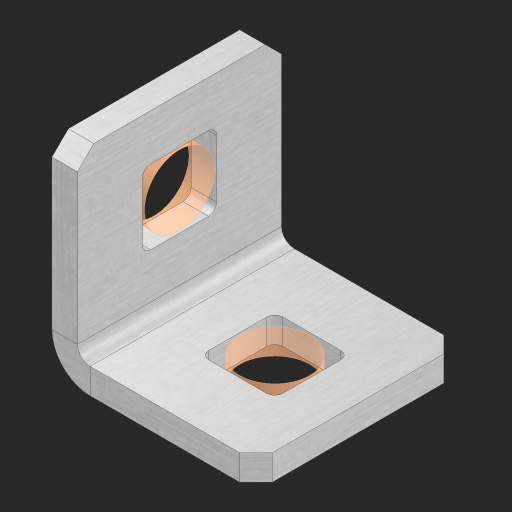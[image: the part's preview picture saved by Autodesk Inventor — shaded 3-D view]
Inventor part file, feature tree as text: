
AUTODESK INVENTOR PART (.ipt)
format: ipt  version: 2023 (Build 270158000, 158)  size: 431,104 bytes
history: native  units: in
note: dims shown in document units (in); Inventor stores cm internally (conversion verified against a paired STEP export)
features: other x76, extrude x71, sheet_metal_op x8, sketch x5, pattern_linear x1, mirror x1, chamfer x1
ambient origin geometry x8: Origin, YZ Plane, XZ Plane, XY Plane, X Axis, Y Axis, Z Axis, Center Point
bodies: Solid1 (feature_tree), Body (feature_tree)
feature tree (163):
  sheet_metal_op  "Flanges"
  sheet_metal_op  "Body Pattern"
  other  "Arc Length"
  pattern_linear  "Notch Pattern"  Spacing1=0.125in  [1 undecoded]
  other  "Diagonal Plane"
  mirror  "Everything Mirrored"
  chamfer  "End Chamfer"
  sketch  "Sketch1"  dims[d0=0.5in]
  other  "Plate1"
  sketch  "Sketch2"  dims[d1=0.5in]
  other  "Plate2"
  sheet_metal_op  "Bend1"
  sheet_metal_op  "Corner1"
  sketch  "Sketch8"  dims[d2=0.0625in]
  sketch  "Sketch9"  dims[d3=0.0625in]
  other  "Srf91"
  sheet_metal_op  "Body Pattern Sketch"
  other  "Srf92"
  sketch  "Sketch13"  dims[d4=0.0312in d5=0.125in d6=0.0625in d7=0.5in d8=90.0deg d9=0.0312in d10=0.25in d11=0.0625in d12=0.0625in d49=0.182in d50=0.02in d52=0.25in d53=0.0625in d54=0.0in d55=0.172in d56=1.0in d57=0.0in d85=0.1473in d86=0.1782in d89=0.0625in d90=0.0in d91=0.04in d92=0.0491in d95=2.5in d96=0.04in d97=0.25in d98=45.0deg d123=0.204in d126=0.0491in d127=0.1473in d128=0.08in d129=0.04in d130=2.5in d131=0.3937in d133=0.5in d134=0.3937in d136=1.0in]
  other  "Srf856"
  other  "Srf857"
  other  "Srf858"
  other  "Srf859"
  other  "Srf860"
  other  "Srf861"
  other  "Srf1275"
  other  "Srf1276"
  other  "Srf1278"
  other  "Srf1279"
  other  "Srf1280"
  other  "Srf1281"
  other  "Srf1282"
  other  "Srf1283"
  other  "Srf1383"
  other  "Srf1384"
  other  "Srf1385"
  other  "Srf1386"
  other  "Srf1387"
  other  "Srf1388"
  other  "Srf1389"
  other  "Srf1390"
  other  "Srf1391"
  other  "Srf1392"
  other  "Srf1393"
  other  "Srf1394"
  other  "Srf1395"
  other  "Srf1396"
  other  "Srf1397"
  other  "Srf1398"
  other  "Srf1399"
  other  "Srf1400"
  other  "Srf1401"
  other  "Srf1402"
  other  "Srf1403"
  other  "Srf1404"
  other  "Srf1405"
  other  "Srf1406"
  other  "Srf1407"
  other  "Srf1408"
  other  "Srf1409"
  other  "Srf1475"
  other  "Srf1476"
  other  "Srf1477"
  other  "Srf1478"
  other  "Srf1479"
  other  "Srf1480"
  other  "Srf1481"
  other  "Srf1482"
  other  "Srf1483"
  other  "Srf1484"
  other  "Srf1485"
  other  "Srf1486"
  other  "Srf1487"
  other  "Srf1488"
  other  "Srf1489"
  other  "Srf1490"
  other  "Srf1491"
  other  "Srf1492"
  other  "Srf1493"
  other  "Srf1494"
  other  "Srf1495"
  other  "Srf1496"
  other  "Srf1497"
  other  "Srf1498"
  other  "Srf1499"
  other  "Srf1500"
  other  "Srf1501"
  other  "Srf1568"
  other  "Srf1569"
  sheet_metal_op  "Body Stamp"
  sheet_metal_op  "Body Circle"
  sheet_metal_op  "Notch"
  extrude  "ExtrusionSrf92"  Depth=0.0625in
  extrude  "ExtrusionSrf856"  Depth=0.5in TaperAngle=90.0deg
  extrude  "ExtrusionSrf857"  Depth=0.25in
  extrude  "ExtrusionSrf858"  Depth=0.0625in
  extrude  "ExtrusionSrf859"  Depth=0.0625in
  extrude  "ExtrusionSrf860"  Depth=0.182in
  extrude  "ExtrusionSrf861"  Depth=0.02in
  extrude  "ExtrusionSrf1275"  Depth=0.25in
  extrude  "ExtrusionSrf1276"  Depth=0.0625in
  extrude  "ExtrusionSrf1277"  TaperAngle=0.0deg  [1 undecoded]
  extrude  "ExtrusionSrf1278"  Depth=0.3937in
  extrude  "ExtrusionSrf1279"  Depth=0.3937in TaperAngle=0.0deg
  extrude  "ExtrusionSrf1280"  Depth=0.3937in
  extrude  "ExtrusionSrf1281"  Depth=0.3937in
  extrude  "ExtrusionSrf1282"  Depth=0.0625in
  extrude  "ExtrusionSrf1383"  Depth=0.3937in TaperAngle=0.0deg
  extrude  "ExtrusionSrf1384"  Depth=0.3937in
  extrude  "ExtrusionSrf1385"  Depth=0.25in TaperAngle=45.0deg
  extrude  "ExtrusionSrf1386"  Depth=0.3937in
  extrude  "ExtrusionSrf1387"  Depth=0.3937in
  extrude  "ExtrusionSrf1388"  Depth=0.3937in
  extrude  "ExtrusionSrf1389"  Depth=0.3937in
  extrude  "ExtrusionSrf1390"  Depth=0.3937in
  extrude  "ExtrusionSrf1391"  Depth=0.3937in
  extrude  "ExtrusionSrf1392"  Depth=0.3937in
  extrude  "ExtrusionSrf1393"  Depth=0.5in
  extrude  "ExtrusionSrf1394"  [1 undecoded]
  extrude  "ExtrusionSrf1395"  [1 undecoded]
  extrude  "ExtrusionSrf1396"  [1 undecoded]
  extrude  "ExtrusionSrf1397"  [1 undecoded]
  extrude  "ExtrusionSrf1398"  [1 undecoded]
  extrude  "ExtrusionSrf1399"  [1 undecoded]
  extrude  "ExtrusionSrf1400"  [1 undecoded]
  extrude  "ExtrusionSrf1401"  [1 undecoded]
  extrude  "ExtrusionSrf1402"  [1 undecoded]
  extrude  "ExtrusionSrf1403"  [1 undecoded]
  extrude  "ExtrusionSrf1404"  [1 undecoded]
  extrude  "ExtrusionSrf1405"  [1 undecoded]
  extrude  "ExtrusionSrf1406"  [1 undecoded]
  extrude  "ExtrusionSrf1407"  [1 undecoded]
  extrude  "ExtrusionSrf1408"  [1 undecoded]
  extrude  "ExtrusionSrf1409"  [1 undecoded]
  extrude  "ExtrusionSrf1475"  [1 undecoded]
  extrude  "ExtrusionSrf1476"  [1 undecoded]
  extrude  "ExtrusionSrf1477"  [1 undecoded]
  extrude  "ExtrusionSrf1478"  [1 undecoded]
  extrude  "ExtrusionSrf1479"  [1 undecoded]
  extrude  "ExtrusionSrf1480"  [1 undecoded]
  extrude  "ExtrusionSrf1481"  [1 undecoded]
  extrude  "ExtrusionSrf1482"  [1 undecoded]
  extrude  "ExtrusionSrf1483"  [1 undecoded]
  extrude  "ExtrusionSrf1484"  [1 undecoded]
  extrude  "ExtrusionSrf1485"  [1 undecoded]
  extrude  "ExtrusionSrf1486"  [1 undecoded]
  extrude  "ExtrusionSrf1487"  [1 undecoded]
  extrude  "ExtrusionSrf1488"  [1 undecoded]
  extrude  "ExtrusionSrf1489"  [1 undecoded]
  extrude  "ExtrusionSrf1490"  [1 undecoded]
  extrude  "ExtrusionSrf1491"  [1 undecoded]
  extrude  "ExtrusionSrf1492"  [1 undecoded]
  extrude  "ExtrusionSrf1493"  [1 undecoded]
  extrude  "ExtrusionSrf1494"  [1 undecoded]
  extrude  "ExtrusionSrf1495"  [1 undecoded]
  extrude  "ExtrusionSrf1496"  [1 undecoded]
  extrude  "ExtrusionSrf1497"  [1 undecoded]
  extrude  "ExtrusionSrf1498"  [1 undecoded]
  extrude  "ExtrusionSrf1499"  [1 undecoded]
  extrude  "ExtrusionSrf1500"  [1 undecoded]
  extrude  "ExtrusionSrf1501"  [1 undecoded]
  extrude  "ExtrusionSrf1568"  [1 undecoded]
  extrude  "ExtrusionSrf1569"  [1 undecoded]
note: 47 required parameter values undecoded (feature->parameter linkage not recoverable at this tier; creation-order binding heuristic only, values carry confidence <= 0.55)
